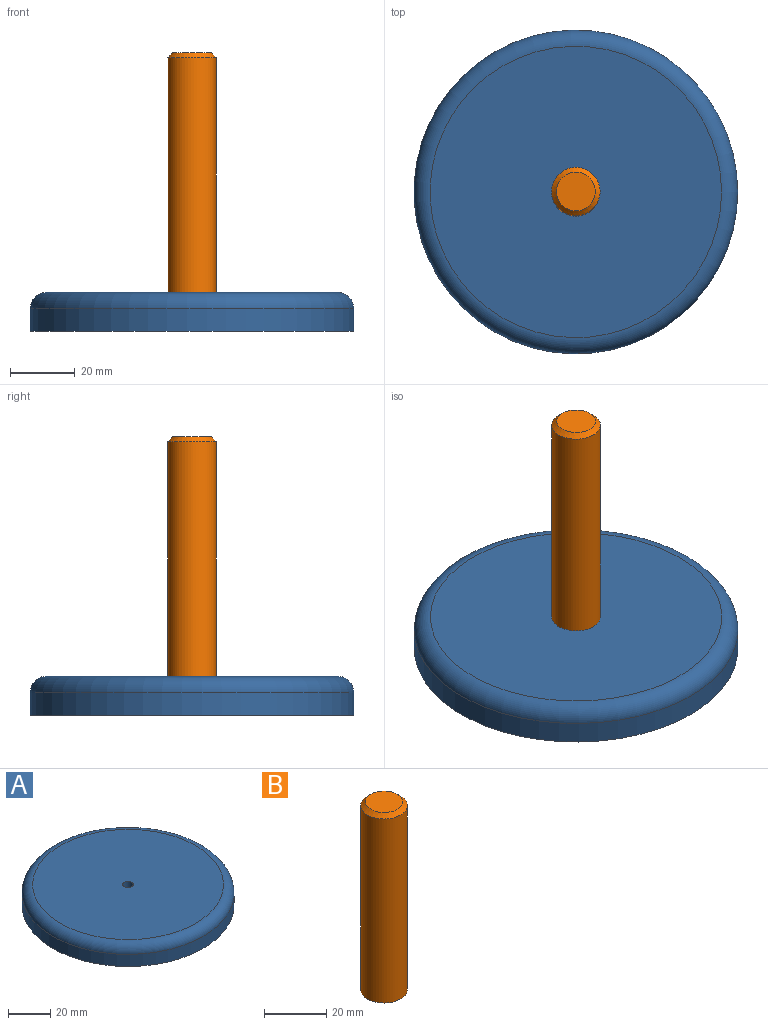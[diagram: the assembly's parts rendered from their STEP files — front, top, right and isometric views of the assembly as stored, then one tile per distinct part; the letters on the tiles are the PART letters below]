
ASSEMBLY  parts=2 mates=1
PART A: 6 faces, bbox 108.2x108.2x12 mm
  f0: plane 90x90mm, normal (0,0,1), area 6342.1mm2, adj f3,f5
  f1: cylinder r=50mm len=100mm, axis (0,0,-1), area 2199.1mm2, adj f2,f5
  f2: plane 100x100mm, normal (0,0,-1), area 7775.4mm2, adj f1,f4
  f3: cylinder r=2.5mm len=9.5mm, axis (0,0,-1), area 149.2mm2, adj f0,f4
  f4: cone r=2.5mm half-angle=45deg, axis (0,0,-1), area 83.3mm2, adj f2,f3
  f5: torus R=45mm, axis (0,0,1), area 2377.7mm2, adj f0,f1
PART B: 6 faces, bbox 15x15x74 mm
  f0: cylinder r=7.5mm len=72.5mm, axis (0,0,-1), area 3416.5mm2, adj f2,f5
  f1: plane 12x12mm, normal (0,0,1), area 113.1mm2, adj f5
  f2: plane 15x15mm, normal (0,0,-1), area 157.1mm2, adj f0,f4
  f3: cone r=0mm half-angle=59deg, axis (0,0,-1), area 22.9mm2, adj f4
  f4: cylinder r=2.5mm len=12mm, axis (0,0,-1), area 188.5mm2, adj f2,f3
  f5: cone r=6mm half-angle=45deg, axis (0,0,-1), area 90mm2, adj f0,f1
PLACE A t=(0.05,0.12,-5.87)mm
PLACE B t=(0.05,0.12,0)mm
MATE slider B.f0 <-> A.f1  axis (0,0,-1) through (0.05,0.12,6.13)mm
